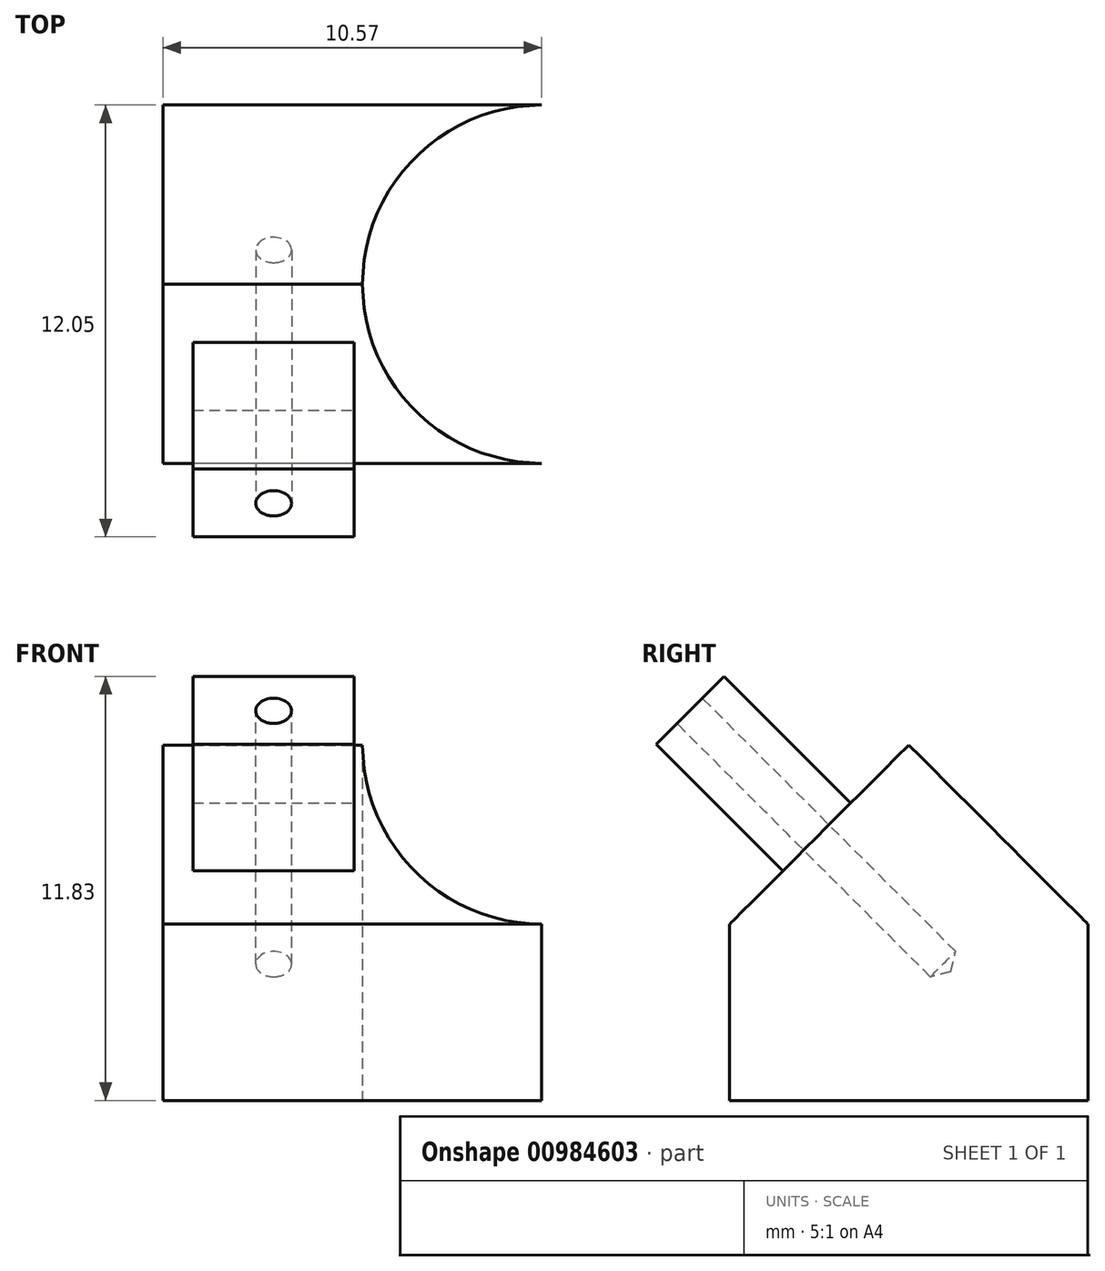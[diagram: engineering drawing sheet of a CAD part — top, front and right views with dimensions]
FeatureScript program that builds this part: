
annotation { "Feature Type Name" : "Feature", "Feature Type Description" : "" }
export const myFeature = defineFeature(function(context is Context, id is Id, definition is map)
    precondition{}
    {
        {
            var Q0;
            Q0=qCreatedBy(makeId("Top.planeOp"),FACE);
            var sketch = newSketch(context, id + "F0", { "sketchPlane" : qUnion([Q0])});
            skCircle(sketch, "E0", {"center": v(0, 0) * mm, "radius": 5 * mm});
            skLineSegment(sketch, "E1.bottom", {"start": v(0, 5) * mm, "end": v(-10.57, 5) * mm});
            skLineSegment(sketch, "E1.top", {"start": v(0, -5) * mm, "end": v(-10.57, -5) * mm});
            skLineSegment(sketch, "E1.left", {"start": v(0, 5) * mm, "end": v(0, -5) * mm});
            skLineSegment(sketch, "E1.right", {"start": v(-10.57, 5) * mm, "end": v(-10.57, -5) * mm});
            skSolve(sketch);
        }
        {
            var Q0;
            {var subQ1=sQuery(id+"F0.wireOp",EDGE,"E1.bottom");Q0=makeQuery(id+"F0.imprint","IMPRINT",FACE,{"disambiguationData":[TD([[makeQuery(id+"F0.imprint","IMPRINT",EDGE,{"derivedFrom":subQ1}),1.0]])]});}
            extrude(context, id + "F1", {"entities" : qUnion([Q0]), "depth" : 10 * mm, "offsetDistance" : 25.4 * mm});
        }
        {
            var Q0;
            Q0=makeQuery(id+"F1.opExtrude","CAP_EDGE",EDGE,{"disambiguationData":[OSD([sQuery(id+"F0.wireOp",EDGE,"E1.top")])],"isStart":false});
            var Q1;
            Q1=makeQuery(id+"F1.opExtrude","CAP_EDGE",EDGE,{"disambiguationData":[OSD([sQuery(id+"F0.wireOp",EDGE,"E1.bottom")])],"isStart":false});
            chamfer(context, id + "F2", {"entities" : qUnion([Q0, Q1]), "width" : 5.08 * mm, "tangentPropagation" : true});
        }
        {
            var Q0;
            Q0=makeQuery(id+"F2.opChamfer","BLEND_FACE",FACE,{"disambiguationData":[OSD([sQuery(id+"F0.wireOp",EDGE,"E1.top")])]});
            var sketch = newSketch(context, id + "F3", { "sketchPlane" : qUnion([Q0])});
            skLineSegment(sketch, "E2.bottom", {"start": v(-9.73, 4.72) * mm, "end": v(-5.23, 4.72) * mm});
            skLineSegment(sketch, "E2.top", {"start": v(-9.73, 2.04) * mm, "end": v(-5.23, 2.04) * mm});
            skLineSegment(sketch, "E2.left", {"start": v(-9.73, 4.72) * mm, "end": v(-9.73, 2.04) * mm});
            skLineSegment(sketch, "E2.right", {"start": v(-5.23, 4.72) * mm, "end": v(-5.23, 2.04) * mm});
            skSolve(sketch);
        }
        {
            var Q0;
            Q0=makeQuery(id+"F3.imprint","IMPRINT",FACE,{"disambiguationData":[TD([[makeQuery(id+"F3.imprint","IMPRINT",EDGE,{"derivedFrom":sQuery(id+"F3.wireOp",EDGE,"E2.bottom")}),-1.0]])]});
            extrude(context, id + "F4", {"entities" : qUnion([Q0]), "operationType" : NewBodyOperationType.ADD, "depth" : 5 * mm, "offsetDistance" : 25.4 * mm});
        }
        {
            var Q0;
            Q0=makeQuery(id+"F4.opExtrude","CAP_FACE",FACE,{"disambiguationData":[OSD([sQuery(id+"F3.wireOp",EDGE,"E2.bottom"),sQuery(id+"F3.wireOp",EDGE,"E2.top"),sQuery(id+"F3.wireOp",EDGE,"E2.left"),sQuery(id+"F3.wireOp",EDGE,"E2.right")])],"isStart":false});
            var sketch = newSketch(context, id + "F5", { "sketchPlane" : qUnion([Q0])});
            skCircle(sketch, "E3", {"center": v(-7.48, 3.36) * mm, "radius": 0.76 * mm});
            skSolve(sketch);
        }
        {
            var Q0;
            Q0=sQuery(id+"F5.wireOp",VERTEX,"E3.center");
            var Q1;
            Q1=makeQuery(id+"F1.opExtrude","SWEPT_BODY",BODY,{"disambiguationData":[OSD([sQuery(id+"F0.wireOp",EDGE,"E0"),sQuery(id+"F0.wireOp",EDGE,"E1.bottom"),sQuery(id+"F0.wireOp",EDGE,"E1.top"),sQuery(id+"F0.wireOp",EDGE,"E1.right")])]});
            hole(context, id + "F6", {"style" : HoleStyle.SIMPLE, "endStyle" : HoleEndStyle.BLIND, "holeDiameter" : 1 * mm, "majorDiameter" : 6.35 * mm, "holeDepth" : 10 * mm, "isTappedThrough" : true, "tappedDepth" : 12.7 * mm, "tapClearance" : 3, "locations" : qUnion([Q0]), "scope" : qUnion([Q1])});
        }
    });
